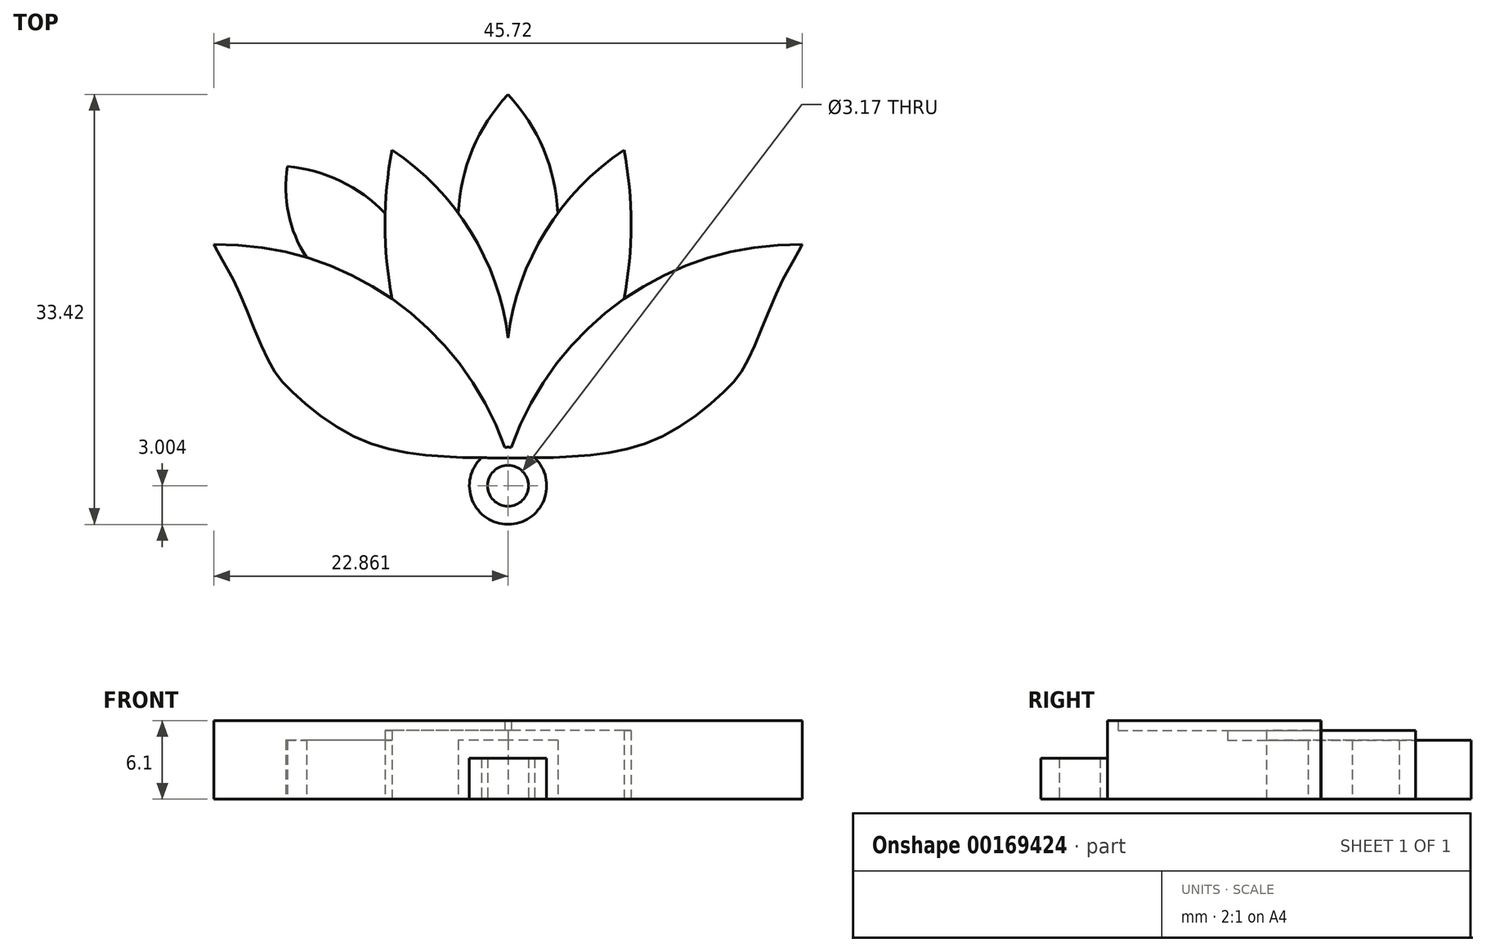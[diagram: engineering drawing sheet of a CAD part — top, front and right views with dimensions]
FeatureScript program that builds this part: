
annotation { "Feature Type Name" : "Feature", "Feature Type Description" : "" }
export const myFeature = defineFeature(function(context is Context, id is Id, definition is map)
    precondition{}
    {
        {
            var Q0;
            Q0=qCreatedBy(makeId("Top.planeOp"),FACE);
            var sketch = newSketch(context, id + "F0", { "sketchPlane" : qUnion([Q0])});
            skArc(sketch, "E0", {"start": v(-0.29, 15.6) * mm, "mid": v(-3.05, 11.34) * mm, "end": v(-4.15, 6.38) * mm});
            skArc(sketch, "E1", {"start": v(-9.84, 6.38) * mm, "mid": v(-13.31, 8.88) * mm, "end": v(-17.43, 10.02) * mm});
            skArc(sketch, "E2", {"start": v(-17.43, 10.02) * mm, "mid": v(-17.35, 6.34) * mm, "end": v(-15.95, 2.94) * mm});
            skFitSpline(sketch, "E3.MirrorCS", {"points": [v(22.57, 3.95) * mm, v(21.97, 2.85) * mm, v(20.68, 0.42) * mm, v(18.47, -4.8) * mm, v(16.62, -7.38) * mm, v(11.7, -10.96) * mm, v(5.86, -12.44) * mm, v(-0.29, -12.63) * mm], "startDerivative": vector(-6.44, -11.3) * mm, "endDerivative": vector(-35.94, 0.04) * mm});
            skArc(sketch, "E4", {"start": v(-9.3, 11.3) * mm, "mid": v(-9.85, 5.51) * mm, "end": v(-9.3, -0.28) * mm});
            skArc(sketch, "E5", {"start": v(-0.29, -3.32) * mm, "mid": v(-3.2, 4.98) * mm, "end": v(-9.3, 11.3) * mm});
            skArc(sketch, "E6.MirrorCS", {"start": v(-0.29, 15.6) * mm, "mid": v(2.47, 11.34) * mm, "end": v(3.57, 6.38) * mm});
            skArc(sketch, "E7.MirrorCS", {"start": v(-0.29, -3.32) * mm, "mid": v(2.62, 4.98) * mm, "end": v(8.73, 11.3) * mm});
            skArc(sketch, "E8.MirrorCS", {"start": v(8.73, 11.3) * mm, "mid": v(9.27, 5.51) * mm, "end": v(8.73, -0.28) * mm});
            skArc(sketch, "E9.MirrorCS", {"start": v(9.26, 6.38) * mm, "mid": v(12.73, 8.88) * mm, "end": v(16.85, 10.02) * mm});
            skArc(sketch, "E10.MirrorCS", {"start": v(16.85, 10.02) * mm, "mid": v(16.77, 6.34) * mm, "end": v(15.37, 2.94) * mm});
            skCircle(sketch, "E11", {"center": v(-0.29, -14.8) * mm, "radius": 1.59 * mm});
            skArc(sketch, "E12", {"start": v(22.57, 3.95) * mm, "mid": v(8.37, -0.53) * mm, "end": v(-0.29, -12.63) * mm});
            skFitSpline(sketch, "E13.MirrorCS", {"points": [v(-23.15, 3.95) * mm, v(-22.55, 2.85) * mm, v(-21.26, 0.42) * mm, v(-19.05, -4.8) * mm, v(-17.2, -7.38) * mm, v(-12.27, -10.96) * mm, v(-6.44, -12.44) * mm, v(-0.29, -12.63) * mm], "startDerivative": vector(6.44, -11.3) * mm, "endDerivative": vector(35.94, 0.04) * mm});
            skArc(sketch, "E14", {"start": v(-0.29, -12.63) * mm, "mid": v(-8.95, -0.53) * mm, "end": v(-23.15, 3.95) * mm});
            skCircle(sketch, "E15", {"center": v(-0.29, -14.8) * mm, "radius": 3 * mm});
            skSolve(sketch);
        }
        {
            var Q0;
            {var subQ0=sQuery(id+"F0.wireOp",EDGE,"E0");Q0=makeQuery(id+"F0.imprint","IMPRINT",FACE,{"disambiguationData":[TD([[makeQuery(id+"F0.imprint","IMPRINT",EDGE,{"derivedFrom":subQ0}),1.0]])]});}
            var Q1;
            {var subQ3=sQuery(id+"F0.wireOp",EDGE,"E9.MirrorCS");Q1=makeQuery(id+"F0.imprint","IMPRINT",FACE,{"disambiguationData":[TD([[makeQuery(id+"F0.imprint","IMPRINT",EDGE,{"derivedFrom":subQ3}),-1.0]])]});}
            var Q2;
            {var subQ0=sQuery(id+"F0.wireOp",EDGE,"E1");Q2=makeQuery(id+"F0.imprint","IMPRINT",FACE,{"disambiguationData":[TD([[makeQuery(id+"F0.imprint","IMPRINT",EDGE,{"derivedFrom":subQ0}),1.0]])]});}
            extrude(context, id + "F1", {"entities" : qUnion([Q0, Q1, Q2]), "depth" : 4.57 * mm});
        }
        {
            var Q0;
            {var subQ2=sQuery(id+"F0.wireOp",EDGE,"E4");var subQ6=makeQuery(id+"F0.imprint","INTERSECT",VERTEX,{"derivedFrom":[sQuery(id+"F0.wireOp",EDGE,"E1"),subQ2]});Q0=makeQuery(id+"F0.imprint","IMPRINT",FACE,{"disambiguationData":[TD([[makeQuery(id+"F0.imprint","IMPRINT",EDGE,{"disambiguationData":[TD([[subQ6,1.0]])],"derivedFrom":subQ2}),1.0]])]});}
            extrude(context, id + "F2", {"entities" : qUnion([Q0]), "operationType" : NewBodyOperationType.ADD, "depth" : 5.33 * mm});
        }
        {
            var Q0;
            {var subQ0=sQuery(id+"F0.wireOp",EDGE,"E12");var subQ3=sQuery(id+"F0.wireOp",EDGE,"E3.MirrorCS");var subQ6=makeQuery(id+"F0.imprint","INTERSECT",VERTEX,{"derivedFrom":[subQ3,subQ0]});Q0=makeQuery(id+"F0.imprint","IMPRINT",FACE,{"disambiguationData":[TD([[makeQuery(id+"F0.imprint","IMPRINT",EDGE,{"disambiguationData":[TD([[subQ6,-1.0]])],"derivedFrom":subQ3}),-1.0]])]});}
            extrude(context, id + "F3", {"entities" : qUnion([Q0]), "operationType" : NewBodyOperationType.ADD, "depth" : 6.1 * mm});
        }
        {
            var Q0;
            {var subQ3=sQuery(id+"F0.wireOp",EDGE,"E13.MirrorCS");var subQ5=makeQuery(id+"F0.imprint","INTERSECT",VERTEX,{"derivedFrom":[sQuery(id+"F0.wireOp",EDGE,"iTXZ8ifU-o21p-C9ul-tzXM-5zlgsoZmCHoD"),subQ3]});Q0=makeQuery(id+"F0.imprint","IMPRINT",FACE,{"disambiguationData":[TD([[makeQuery(id+"F0.imprint","IMPRINT",EDGE,{"disambiguationData":[TD([[subQ5,1.0]])],"derivedFrom":subQ3}),1.0]])]});}
            var Q1;
            {var subQ1=sQuery(id+"F0.wireOp",EDGE,"E3.MirrorCS");var subQ3=sQuery(id+"F0.wireOp",EDGE,"E15");var subQ4=makeQuery(id+"F0.imprint","INTERSECT",VERTEX,{"derivedFrom":[subQ1,subQ3]});Q1=makeQuery(id+"F0.imprint","IMPRINT",FACE,{"disambiguationData":[TD([[makeQuery(id+"F0.imprint","IMPRINT",EDGE,{"disambiguationData":[TD([[subQ4,-1.0]])],"derivedFrom":subQ3}),1.0]])]});}
            var Q2;
            {var subQ1=sQuery(id+"F0.wireOp",EDGE,"E12");var subQ3=sQuery(id+"F0.wireOp",EDGE,"E15");var subQ4=makeQuery(id+"F0.imprint","INTERSECT",VERTEX,{"derivedFrom":[subQ1,subQ3]});Q2=makeQuery(id+"F0.imprint","IMPRINT",FACE,{"disambiguationData":[TD([[makeQuery(id+"F0.imprint","IMPRINT",EDGE,{"disambiguationData":[TD([[subQ4,-1.0]])],"derivedFrom":subQ3}),1.0]])]});}
            var Q3;
            {var subQ1=sQuery(id+"F0.wireOp",EDGE,"E13.MirrorCS");var subQ3=sQuery(id+"F0.wireOp",EDGE,"E15");var subQ4=makeQuery(id+"F0.imprint","INTERSECT",VERTEX,{"derivedFrom":[subQ1,subQ3]});Q3=makeQuery(id+"F0.imprint","IMPRINT",FACE,{"disambiguationData":[TD([[makeQuery(id+"F0.imprint","IMPRINT",EDGE,{"disambiguationData":[TD([[subQ4,1.0]])],"derivedFrom":subQ3}),1.0]])]});}
            extrude(context, id + "F4", {"entities" : qUnion([Q0, Q1, Q2, Q3]), "depth" : 6.1 * mm});
        }
        {
            var Q0;
            {var subQ1=sQuery(id+"F0.wireOp",EDGE,"E3.MirrorCS");var subQ3=sQuery(id+"F0.wireOp",EDGE,"E15");var subQ4=makeQuery(id+"F0.imprint","INTERSECT",VERTEX,{"derivedFrom":[subQ1,subQ3]});Q0=makeQuery(id+"F0.imprint","IMPRINT",FACE,{"disambiguationData":[TD([[makeQuery(id+"F0.imprint","IMPRINT",EDGE,{"disambiguationData":[TD([[subQ4,-1.0]])],"derivedFrom":subQ3}),1.0]])]});}
            var Q1;
            Q1=makeQuery(id+"F0.imprint","IMPRINT",FACE,{"disambiguationData":[TD([[makeQuery(id+"F0.imprint","IMPRINT",EDGE,{"derivedFrom":sQuery(id+"F0.wireOp",EDGE,"E11")}),-1.0]])]});
            var Q2;
            {var subQ1=sQuery(id+"F0.wireOp",EDGE,"E13.MirrorCS");var subQ3=sQuery(id+"F0.wireOp",EDGE,"E15");var subQ4=makeQuery(id+"F0.imprint","INTERSECT",VERTEX,{"derivedFrom":[subQ1,subQ3]});Q2=makeQuery(id+"F0.imprint","IMPRINT",FACE,{"disambiguationData":[TD([[makeQuery(id+"F0.imprint","IMPRINT",EDGE,{"disambiguationData":[TD([[subQ4,1.0]])],"derivedFrom":subQ3}),1.0]])]});}
            var Q3;
            {var subQ1=sQuery(id+"F0.wireOp",EDGE,"E12");var subQ3=sQuery(id+"F0.wireOp",EDGE,"E15");var subQ4=makeQuery(id+"F0.imprint","INTERSECT",VERTEX,{"derivedFrom":[subQ1,subQ3]});Q3=makeQuery(id+"F0.imprint","IMPRINT",FACE,{"disambiguationData":[TD([[makeQuery(id+"F0.imprint","IMPRINT",EDGE,{"disambiguationData":[TD([[subQ4,-1.0]])],"derivedFrom":subQ3}),1.0]])]});}
            extrude(context, id + "F5", {"entities" : qUnion([Q0, Q1, Q2, Q3]), "operationType" : NewBodyOperationType.ADD, "depth" : 3.17 * mm});
        }
    });
